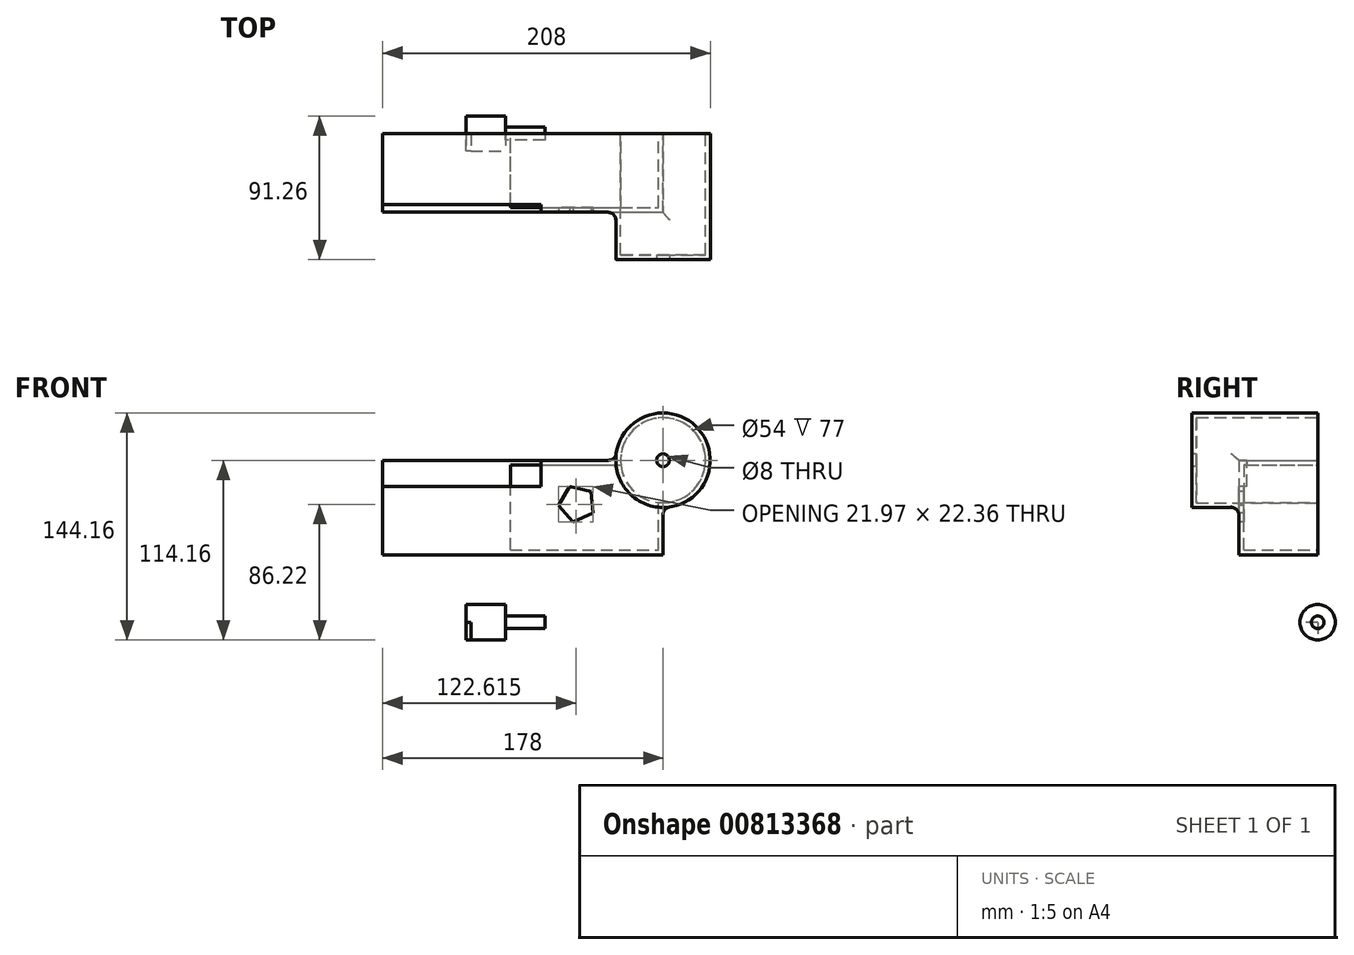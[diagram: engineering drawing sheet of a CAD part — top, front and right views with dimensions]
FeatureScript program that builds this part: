
annotation { "Feature Type Name" : "Feature", "Feature Type Description" : "" }
export const myFeature = defineFeature(function(context is Context, id is Id, definition is map)
    precondition{}
    {
        {
            var Q0;
            Q0=qCreatedBy(makeId("Front.planeOp"),FACE);
            var sketch = newSketch(context, id + "F0", { "sketchPlane" : qUnion([Q0])});
            skLineSegment(sketch, "E0.bottom", {"start": v(0, 0) * mm, "end": v(100, 0) * mm});
            skLineSegment(sketch, "E0.top", {"start": v(0, 60) * mm, "end": v(100, 60) * mm});
            skLineSegment(sketch, "E0.left", {"start": v(0, 0) * mm, "end": v(0, 60) * mm});
            skLineSegment(sketch, "E0.right", {"start": v(100, 0) * mm, "end": v(100, 60) * mm});
            skCircle(sketch, "E1", {"center": v(100, 60) * mm, "radius": 30 * mm});
            skSolve(sketch);
        }
        {
            var Q0;
            {var subQ1=sQuery(id+"F0.wireOp",EDGE,"E0.bottom");Q0=makeQuery(id+"F0.imprint","IMPRINT",FACE,{"disambiguationData":[TD([[makeQuery(id+"F0.imprint","IMPRINT",EDGE,{"derivedFrom":subQ1}),1.0]])]});}
            var Q1;
            {var subQ0=sQuery(id+"F0.wireOp",EDGE,"E0.right");var subQ1=sQuery(id+"F0.wireOp",EDGE,"E0.top");var subQ2=makeQuery(id+"F0.imprint","INTERSECT",VERTEX,{"derivedFrom":[subQ1,subQ0]});Q1=makeQuery(id+"F0.imprint","IMPRINT",FACE,{"disambiguationData":[TD([[makeQuery(id+"F0.imprint","IMPRINT",EDGE,{"disambiguationData":[TD([[subQ2,1.0]])],"derivedFrom":subQ1}),-1.0]])]});}
            extrude(context, id + "F1", {"entities" : qUnion([Q0, Q1]), "depth" : 50 * mm, "offsetDistance" : 25 * mm});
        }
        {
            var Q0;
            {var subQ0=sQuery(id+"F0.wireOp",EDGE,"E0.right");var subQ1=sQuery(id+"F0.wireOp",EDGE,"E0.top");var subQ2=makeQuery(id+"F0.imprint","INTERSECT",VERTEX,{"derivedFrom":[subQ1,subQ0]});Q0=makeQuery(id+"F0.imprint","IMPRINT",FACE,{"disambiguationData":[TD([[makeQuery(id+"F0.imprint","IMPRINT",EDGE,{"disambiguationData":[TD([[subQ2,1.0]])],"derivedFrom":subQ1}),1.0]])]});}
            var Q1;
            {var subQ0=sQuery(id+"F0.wireOp",EDGE,"E0.right");var subQ1=sQuery(id+"F0.wireOp",EDGE,"E0.top");var subQ2=makeQuery(id+"F0.imprint","INTERSECT",VERTEX,{"derivedFrom":[subQ1,subQ0]});Q1=makeQuery(id+"F0.imprint","IMPRINT",FACE,{"disambiguationData":[TD([[makeQuery(id+"F0.imprint","IMPRINT",EDGE,{"disambiguationData":[TD([[subQ2,1.0]])],"derivedFrom":subQ1}),-1.0]])]});}
            extrude(context, id + "F2", {"entities" : qUnion([Q0, Q1]), "operationType" : NewBodyOperationType.ADD, "depth" : 80 * mm, "offsetDistance" : 25 * mm});
        }
        {
            var Q0;
            Q0=makeQuery(id+"F2.boolean.opBoolean","MERGE",FACE,{"derivedFrom":[makeQuery(id+"F1.opExtrude","CAP_FACE",FACE,{"disambiguationData":[OSD([sQuery(id+"F0.wireOp",EDGE,"E0.bottom"),sQuery(id+"F0.wireOp",EDGE,"E0.top"),sQuery(id+"F0.wireOp",EDGE,"E0.left"),sQuery(id+"F0.wireOp",EDGE,"E0.right")])],"isStart":true}),makeQuery(id+"F2.opExtrude","CAP_FACE",FACE,{"disambiguationData":[OSD([sQuery(id+"F0.wireOp",EDGE,"E1")])],"isStart":true})]});
            shell(context, id + "F3", {"entities" : qUnion([Q0]), "thickness" : 3 * mm});
        }
        {
            var Q0;
            Q0=makeQuery(id+"F2.boolean.opBoolean","INTERSECT",EDGE,{"derivedFrom":[makeQuery(id+"F1.opExtrude","SWEPT_FACE",FACE,{"disambiguationData":[OSD([sQuery(id+"F0.wireOp",EDGE,"E0.top")])]}),makeQuery(id+"F2.opExtrude","SWEPT_FACE",FACE,{"disambiguationData":[OSD([sQuery(id+"F0.wireOp",EDGE,"E1")])]})]});
            var Q1;
            Q1=makeQuery(id+"F2.boolean.opBoolean","INTERSECT",EDGE,{"derivedFrom":[makeQuery(id+"F1.opExtrude","CAP_FACE",FACE,{"disambiguationData":[OSD([sQuery(id+"F0.wireOp",EDGE,"E0.bottom"),sQuery(id+"F0.wireOp",EDGE,"E0.top"),sQuery(id+"F0.wireOp",EDGE,"E0.left"),sQuery(id+"F0.wireOp",EDGE,"E0.right")])],"isStart":false}),makeQuery(id+"F2.opExtrude","SWEPT_FACE",FACE,{"disambiguationData":[OSD([sQuery(id+"F0.wireOp",EDGE,"E1")])]})]});
            var Q2;
            Q2=makeQuery(id+"F2.boolean.opBoolean","INTERSECT",EDGE,{"derivedFrom":[makeQuery(id+"F1.opExtrude","SWEPT_FACE",FACE,{"disambiguationData":[OSD([sQuery(id+"F0.wireOp",EDGE,"E0.right")])]}),makeQuery(id+"F2.opExtrude","SWEPT_FACE",FACE,{"disambiguationData":[OSD([sQuery(id+"F0.wireOp",EDGE,"E1")])]})]});
            fillet(context, id + "F4", {"entities" : qUnion([Q0, Q1, Q2]), "radius" : 5 * mm, "tangentPropagation" : true, "allowEdgeOverflow" : false});
        }
        {
            var Q0;
            Q0=makeQuery(id+"F2.opExtrude","CAP_FACE",FACE,{"disambiguationData":[OSD([sQuery(id+"F0.wireOp",EDGE,"E1")])],"isStart":false});
            var sketch = newSketch(context, id + "F5", { "sketchPlane" : qUnion([Q0])});
            skCircle(sketch, "E2", {"center": v(100, 60) * mm, "radius": 4 * mm});
            skSolve(sketch);
        }
        {
            var Q0;
            Q0=makeQuery(id+"F5.imprint","IMPRINT",FACE,{"disambiguationData":[TD([[makeQuery(id+"F5.imprint","IMPRINT",EDGE,{"derivedFrom":sQuery(id+"F5.wireOp",EDGE,"E2")}),1.0]])]});
            extrude(context, id + "F6", {"entities" : qUnion([Q0]), "operationType" : NewBodyOperationType.REMOVE, "endBound" : BoundingType.THROUGH_ALL, "oppositeDirection" : true, "depth" : 25 * mm, "offsetDistance" : 25 * mm});
        }
        {
            var Q0;
            Q0=qCreatedBy(makeId("Right.planeOp"),FACE);
            var sketch = newSketch(context, id + "F7", { "sketchPlane" : qUnion([Q0])});
            skCircle(sketch, "E3", {"center": v(0, -42.9) * mm, "radius": 4 * mm});
            skSolve(sketch);
        }
        {
            var Q0;
            Q0=makeQuery(id+"F7.imprint","IMPRINT",FACE,{"disambiguationData":[TD([[makeQuery(id+"F7.imprint","IMPRINT",EDGE,{"derivedFrom":sQuery(id+"F7.wireOp",EDGE,"E3")}),1.0]])]});
            extrude(context, id + "F8", {"entities" : qUnion([Q0]), "depth" : 25 * mm, "offsetDistance" : 25 * mm});
        }
        {
            var Q0;
            Q0=makeQuery(id+"F8.opExtrude","CAP_FACE",FACE,{"disambiguationData":[OSD([sQuery(id+"F7.wireOp",EDGE,"E3")])],"isStart":true});
            var sketch = newSketch(context, id + "F9", { "sketchPlane" : qUnion([Q0])});
            skCircle(sketch, "E4", {"center": v(0, -42.9) * mm, "radius": 11.26 * mm});
            skSolve(sketch);
        }
        {
            var Q0;
            Q0=makeQuery(id+"F9.imprint","IMPRINT",FACE,{"disambiguationData":[TD([[makeQuery(id+"F9.imprint","IMPRINT",EDGE,{"derivedFrom":sQuery(id+"F9.wireOp",EDGE,"E4")}),1.0]])]});
            var Q1;
            Q1=makeQuery(id+"F9.imprint","IMPRINT",FACE,{"disambiguationData":[TD([[makeQuery(id+"F9.imprint","IMPRINT",EDGE,{"derivedFrom":makeQuery(id+"F8.opExtrude","CAP_EDGE",EDGE,{"disambiguationData":[OSD([sQuery(id+"F7.wireOp",EDGE,"E3")])],"isStart":true})}),-1.0]])]});
            extrude(context, id + "F10", {"entities" : qUnion([Q0, Q1]), "operationType" : NewBodyOperationType.ADD, "depth" : 25 * mm, "offsetDistance" : 25 * mm});
        }
        {
            var Q0;
            Q0=makeQuery(id+"F10.opExtrude","CAP_FACE",FACE,{"disambiguationData":[OSD([sQuery(id+"F9.wireOp",EDGE,"E4")])],"isStart":false});
            var sketch = newSketch(context, id + "F11", { "sketchPlane" : qUnion([Q0])});
            skLineSegment(sketch, "E5.bottom", {"start": v(0, -42.9) * mm, "end": v(16.38, -42.9) * mm});
            skLineSegment(sketch, "E5.top", {"start": v(0, -64.15) * mm, "end": v(16.38, -64.15) * mm});
            skLineSegment(sketch, "E5.left", {"start": v(0, -42.9) * mm, "end": v(0, -64.15) * mm});
            skLineSegment(sketch, "E5.right", {"start": v(16.38, -42.9) * mm, "end": v(16.38, -64.15) * mm});
            skSolve(sketch);
        }
        {
            var Q0;
            {var subQ0=sQuery(id+"F11.wireOp",EDGE,"E5.left");var subQ1=sQuery(id+"F11.wireOp",EDGE,"E5.bottom");var subQ2=makeQuery(id+"F11.imprint","INTERSECT",VERTEX,{"derivedFrom":[subQ1,subQ0]});Q0=makeQuery(id+"F11.imprint","IMPRINT",FACE,{"disambiguationData":[TD([[makeQuery(id+"F11.imprint","IMPRINT",EDGE,{"disambiguationData":[TD([[subQ2,-1.0]])],"derivedFrom":subQ1}),-1.0]])]});}
            extrude(context, id + "F12", {"entities" : qUnion([Q0]), "operationType" : NewBodyOperationType.REMOVE, "oppositeDirection" : true, "depth" : 3 * mm, "offsetDistance" : 25 * mm});
        }
        {
            var Q0;
            Q0=makeQuery(id+"F1.opExtrude","CAP_FACE",FACE,{"disambiguationData":[OSD([sQuery(id+"F0.wireOp",EDGE,"E0.bottom"),sQuery(id+"F0.wireOp",EDGE,"E0.top"),sQuery(id+"F0.wireOp",EDGE,"E0.left"),sQuery(id+"F0.wireOp",EDGE,"E0.right")])],"isStart":false});
            var sketch = newSketch(context, id + "F13", { "sketchPlane" : qUnion([Q0])});
            skLineSegment(sketch, "E6.bottom", {"start": v(0, 60) * mm, "end": v(22.38, 60) * mm});
            skLineSegment(sketch, "E6.top", {"start": v(0, 43.47) * mm, "end": v(22.38, 43.47) * mm});
            skLineSegment(sketch, "E6.left", {"start": v(0, 60) * mm, "end": v(0, 43.47) * mm});
            skLineSegment(sketch, "E6.right", {"start": v(22.38, 60) * mm, "end": v(22.38, 43.47) * mm});
            skSolve(sketch);
        }
        {
            var Q0;
            Q0=makeQuery(id+"F13.imprint","IMPRINT",FACE,{"disambiguationData":[TD([[makeQuery(id+"F13.imprint","IMPRINT",EDGE,{"derivedFrom":sQuery(id+"F13.wireOp",EDGE,"E6.bottom")}),-1.0]])]});
            extrude(context, id + "F14", {"entities" : qUnion([Q0]), "operationType" : NewBodyOperationType.REMOVE, "oppositeDirection" : true, "depth" : 5 * mm, "offsetDistance" : 25 * mm});
        }
        {
            var Q0;
            Q0=makeQuery(id+"F1.opExtrude","CAP_FACE",FACE,{"disambiguationData":[OSD([sQuery(id+"F0.wireOp",EDGE,"E0.bottom"),sQuery(id+"F0.wireOp",EDGE,"E0.top"),sQuery(id+"F0.wireOp",EDGE,"E0.left"),sQuery(id+"F0.wireOp",EDGE,"E0.right")])],"isStart":false});
            var sketch = newSketch(context, id + "F15", { "sketchPlane" : qUnion([Q0])});
            skCircle(sketch, "E7.cCircle", {"center": v(45.38, 32.43) * mm, "radius": 9.56 * mm, "construction": true});
            skLineSegment(sketch, "E7.0", {"start": v(55.6, 26.5) * mm, "end": v(42.9, 20.88) * mm});
            skLineSegment(sketch, "E7.1", {"start": v(42.9, 20.88) * mm, "end": v(33.63, 31.23) * mm});
            skLineSegment(sketch, "E7.2", {"start": v(33.63, 31.23) * mm, "end": v(40.6, 43.24) * mm});
            skLineSegment(sketch, "E7.3", {"start": v(40.6, 43.24) * mm, "end": v(54.19, 40.31) * mm});
            skLineSegment(sketch, "E7.4", {"start": v(54.19, 40.31) * mm, "end": v(55.6, 26.5) * mm});
            skPoint(sketch, "E7.0.midPoint", {"position": v(49.25, 23.69) * mm});
            skSolve(sketch);
        }
        {
            var Q0;
            Q0=makeQuery(id+"F15.imprint","IMPRINT",FACE,{"disambiguationData":[TD([[makeQuery(id+"F15.imprint","IMPRINT",EDGE,{"derivedFrom":sQuery(id+"F15.wireOp",EDGE,"E7.0")}),-1.0]])]});
            extrude(context, id + "F16", {"entities" : qUnion([Q0]), "operationType" : NewBodyOperationType.REMOVE, "oppositeDirection" : true, "depth" : 25 * mm, "offsetDistance" : 25 * mm});
        }
        {
            var Q0;
            Q0=makeQuery(id+"F1.opExtrude","SWEPT_FACE",FACE,{"disambiguationData":[OSD([sQuery(id+"F0.wireOp",EDGE,"E0.left")])]});
            extrude(context, id + "F17", {"entities" : qUnion([Q0]), "operationType" : NewBodyOperationType.ADD, "depth" : 78 * mm, "offsetDistance" : 25 * mm});
        }
    });
